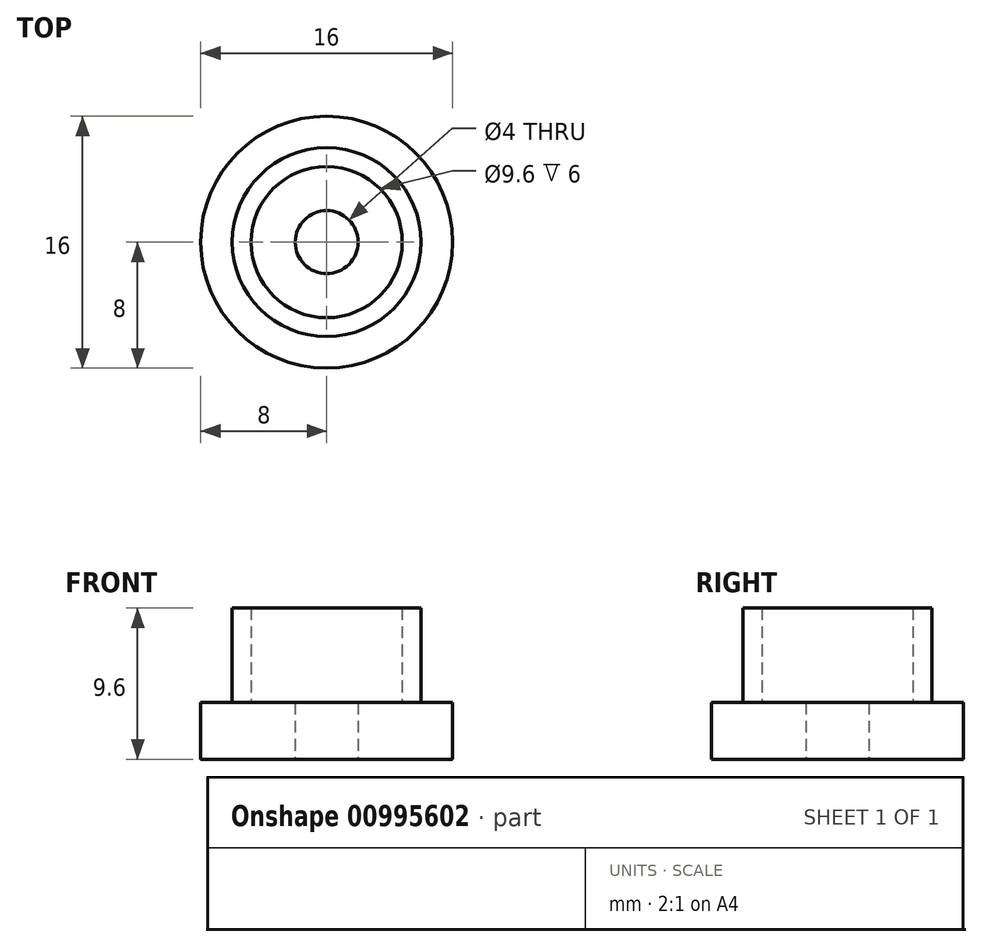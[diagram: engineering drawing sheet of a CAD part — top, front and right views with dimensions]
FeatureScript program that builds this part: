
annotation { "Feature Type Name" : "Feature", "Feature Type Description" : "" }
export const myFeature = defineFeature(function(context is Context, id is Id, definition is map)
    precondition{}
    {
        {
            var Q0;
            Q0=qCreatedBy(makeId("Top.planeOp"),FACE);
            var sketch = newSketch(context, id + "F0", { "sketchPlane" : qUnion([Q0])});
            skCircle(sketch, "E0", {"center": v(0, 0) * mm, "radius": 8 * mm});
            skCircle(sketch, "E1", {"center": v(0, 0) * mm, "radius": 2 * mm});
            skSolve(sketch);
        }
        {
            var Q0;
            Q0=makeQuery(id+"F0.imprint","IMPRINT",FACE,{"disambiguationData":[TD([[makeQuery(id+"F0.imprint","IMPRINT",EDGE,{"derivedFrom":sQuery(id+"F0.wireOp",EDGE,"E0")}),1.0]])]});
            extrude(context, id + "F1", {"entities" : qUnion([Q0]), "depth" : 3.6 * mm, "offsetDistance" : 25 * mm});
        }
        {
            var Q0;
            Q0=makeQuery(id+"F1.opExtrude","CAP_FACE",FACE,{"disambiguationData":[OSD([sQuery(id+"F0.wireOp",EDGE,"E0"),sQuery(id+"F0.wireOp",EDGE,"E1")])],"isStart":false});
            var sketch = newSketch(context, id + "F2", { "sketchPlane" : qUnion([Q0])});
            skCircle(sketch, "E2", {"center": v(0, 0) * mm, "radius": 6 * mm});
            skCircle(sketch, "E3", {"center": v(0, 0) * mm, "radius": 4.8 * mm});
            skSolve(sketch);
        }
        {
            var Q0;
            Q0=makeQuery(id+"F2.imprint","IMPRINT",FACE,{"disambiguationData":[TD([[makeQuery(id+"F2.imprint","IMPRINT",EDGE,{"derivedFrom":sQuery(id+"F2.wireOp",EDGE,"E2")}),1.0]])]});
            extrude(context, id + "F3", {"entities" : qUnion([Q0]), "operationType" : NewBodyOperationType.ADD, "depth" : (9.6 - 3.6) * mm, "offsetDistance" : 25 * mm});
        }
    });
